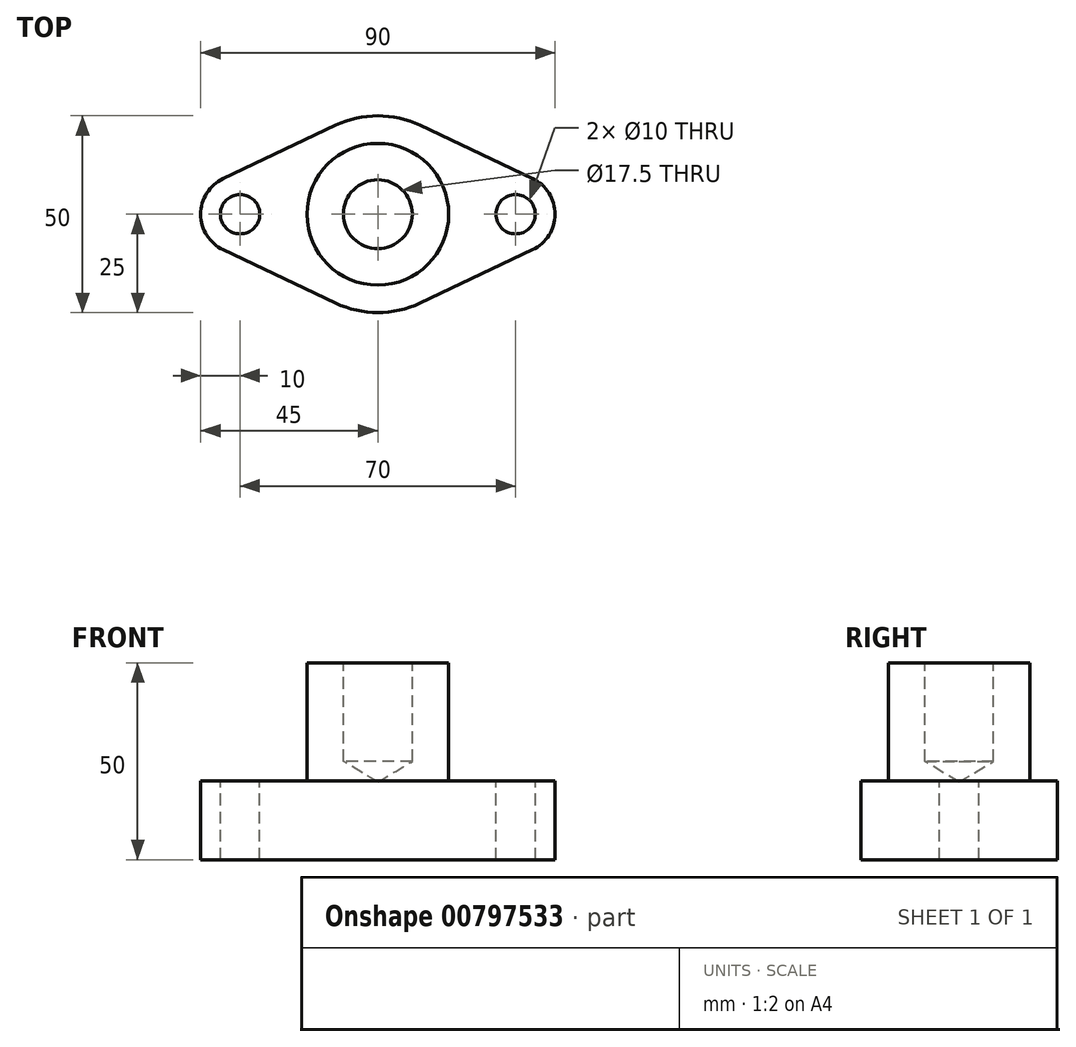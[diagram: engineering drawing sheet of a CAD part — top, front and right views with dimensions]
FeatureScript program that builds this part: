
annotation { "Feature Type Name" : "Feature", "Feature Type Description" : "" }
export const myFeature = defineFeature(function(context is Context, id is Id, definition is map)
    precondition{}
    {
        {
            var Q0;
            Q0=qCreatedBy(makeId("Top.planeOp"),FACE);
            var sketch = newSketch(context, id + "F0", { "sketchPlane" : qUnion([Q0])});
            skLineSegment(sketch, "E0", {"start": v(0, 0) * mm, "end": v(-35, 0) * mm});
            skLineSegment(sketch, "E1", {"start": v(0, 0) * mm, "end": v(35, 0) * mm});
            skArc(sketch, "E2", {"start": v(39.29, -9.04) * mm, "mid": v(45, 0) * mm, "end": v(39.29, 9.04) * mm});
            skArc(sketch, "E3", {"start": v(-39.29, 9.04) * mm, "mid": v(-45, 0) * mm, "end": v(-39.29, -9.04) * mm});
            skArc(sketch, "E4", {"start": v(-10.71, -22.59) * mm, "mid": v(0, -25) * mm, "end": v(10.71, -22.59) * mm});
            skLineSegment(sketch, "E5", {"start": v(-39.29, 9.04) * mm, "end": v(-10.71, 22.59) * mm});
            skLineSegment(sketch, "E6", {"start": v(-39.29, -9.04) * mm, "end": v(-10.71, -22.59) * mm});
            skLineSegment(sketch, "E7", {"start": v(10.71, 22.59) * mm, "end": v(39.29, 9.04) * mm});
            skLineSegment(sketch, "E8", {"start": v(10.71, -22.59) * mm, "end": v(39.29, -9.04) * mm});
            skArc(sketch, "E9.trimOffspring", {"start": v(10.71, 22.59) * mm, "mid": v(0, 25) * mm, "end": v(-10.71, 22.59) * mm});
            skSolve(sketch);
        }
        {
            var Q0;
            Q0=makeQuery(id+"F0.imprint","IMPRINT",FACE,{"disambiguationData":[TD([[makeQuery(id+"F0.imprint","IMPRINT",EDGE,{"derivedFrom":sQuery(id+"F0.wireOp",EDGE,"E2")}),1.0]])]});
            extrude(context, id + "F1", {"entities" : qUnion([Q0]), "depth" : 20 * mm, "offsetDistance" : 25 * mm});
        }
        {
            var Q0;
            Q0=makeQuery(id+"F1.opExtrude","CAP_FACE",FACE,{"disambiguationData":[OSD([sQuery(id+"F0.wireOp",EDGE,"E2"),sQuery(id+"F0.wireOp",EDGE,"E3"),sQuery(id+"F0.wireOp",EDGE,"E4"),sQuery(id+"F0.wireOp",EDGE,"E5"),sQuery(id+"F0.wireOp",EDGE,"E6"),sQuery(id+"F0.wireOp",EDGE,"E7"),sQuery(id+"F0.wireOp",EDGE,"E8"),sQuery(id+"F0.wireOp",EDGE,"E9.trimOffspring")])],"isStart":false});
            var sketch = newSketch(context, id + "F2", { "sketchPlane" : qUnion([Q0])});
            skLineSegment(sketch, "E10", {"start": v(0, 0) * mm, "end": v(35, 0) * mm});
            skLineSegment(sketch, "E11", {"start": v(0, 0) * mm, "end": v(-35, 0) * mm});
            skSolve(sketch);
        }
        {
            var Q0;
            Q0=sQuery(id+"F2.wireOp",VERTEX,"E11.end");
            var Q1;
            Q1=sQuery(id+"F2.wireOp",VERTEX,"E10.end");
            var Q2;
            Q2=makeQuery(id+"F1.opExtrude","SWEPT_BODY",BODY,{"disambiguationData":[OSD([sQuery(id+"F0.wireOp",EDGE,"E2"),sQuery(id+"F0.wireOp",EDGE,"E3"),sQuery(id+"F0.wireOp",EDGE,"E4"),sQuery(id+"F0.wireOp",EDGE,"E5"),sQuery(id+"F0.wireOp",EDGE,"E6"),sQuery(id+"F0.wireOp",EDGE,"E7"),sQuery(id+"F0.wireOp",EDGE,"E8"),sQuery(id+"F0.wireOp",EDGE,"E9.trimOffspring")])]});
            hole(context, id + "F3", {"style" : HoleStyle.SIMPLE, "endStyle" : HoleEndStyle.BLIND, "holeDiameter" : 10 * mm, "majorDiameter" : 5 * mm, "holeDepth" : 20 * mm, "isTappedThrough" : true, "tappedDepth" : 12 * mm, "tapClearance" : 3, "locations" : qUnion([Q0, Q1]), "scope" : qUnion([Q2])});
        }
        {
            var Q0;
            Q0=makeQuery(id+"F1.opExtrude","CAP_FACE",FACE,{"disambiguationData":[OSD([sQuery(id+"F0.wireOp",EDGE,"E2"),sQuery(id+"F0.wireOp",EDGE,"E3"),sQuery(id+"F0.wireOp",EDGE,"E4"),sQuery(id+"F0.wireOp",EDGE,"E5"),sQuery(id+"F0.wireOp",EDGE,"E6"),sQuery(id+"F0.wireOp",EDGE,"E7"),sQuery(id+"F0.wireOp",EDGE,"E8"),sQuery(id+"F0.wireOp",EDGE,"E9.trimOffspring")])],"isStart":false});
            var sketch = newSketch(context, id + "F4", { "sketchPlane" : qUnion([Q0])});
            skCircle(sketch, "E12", {"center": v(0, 0) * mm, "radius": 18 * mm});
            skSolve(sketch);
        }
        {
            var Q0;
            Q0=makeQuery(id+"F4.imprint","IMPRINT",FACE,{"disambiguationData":[TD([[makeQuery(id+"F4.imprint","IMPRINT",EDGE,{"derivedFrom":sQuery(id+"F4.wireOp",EDGE,"E12")}),1.0]])]});
            extrude(context, id + "F5", {"entities" : qUnion([Q0]), "operationType" : NewBodyOperationType.ADD, "depth" : 30 * mm, "offsetDistance" : 25 * mm});
        }
        {
            var Q0;
            Q0=makeQuery(id+"F5.opExtrude","CAP_FACE",FACE,{"disambiguationData":[OSD([sQuery(id+"F4.wireOp",EDGE,"E12")])],"isStart":false});
            var sketch = newSketch(context, id + "F6", { "sketchPlane" : qUnion([Q0])});
            skLineSegment(sketch, "E13", {"start": v(0, 0) * mm, "end": v(1.65, -9.6) * mm});
            skSolve(sketch);
        }
        {
            var Q0;
            Q0=sQuery(id+"F6.wireOp",VERTEX,"E13.start");
            var Q1;
            Q1=makeQuery(id+"F1.opExtrude","SWEPT_BODY",BODY,{"disambiguationData":[OSD([sQuery(id+"F0.wireOp",EDGE,"E2"),sQuery(id+"F0.wireOp",EDGE,"E3"),sQuery(id+"F0.wireOp",EDGE,"E4"),sQuery(id+"F0.wireOp",EDGE,"E5"),sQuery(id+"F0.wireOp",EDGE,"E6"),sQuery(id+"F0.wireOp",EDGE,"E7"),sQuery(id+"F0.wireOp",EDGE,"E8"),sQuery(id+"F0.wireOp",EDGE,"E9.trimOffspring")])]});
            hole(context, id + "F7", {"style" : HoleStyle.SIMPLE, "endStyle" : HoleEndStyle.BLIND, "standardTappedOrClearance" : lookupTablePath({ "standard" : "ISO", "fit" : "Normal", "size" : "M16", "type" : "Clearance" }), "standardBlindInLast" : lookupTablePath({ "fit" : "Standard", "standard" : "ISO", "size" : "M16", "type" : "Clearance" }), "holeDiameter" : 17.5 * mm, "majorDiameter" : 5 * mm, "holeDepth" : 25 * mm, "isTappedThrough" : true, "tappedDepth" : 12 * mm, "tapClearance" : 3, "locations" : qUnion([Q0]), "scope" : qUnion([Q1])});
        }
    });
